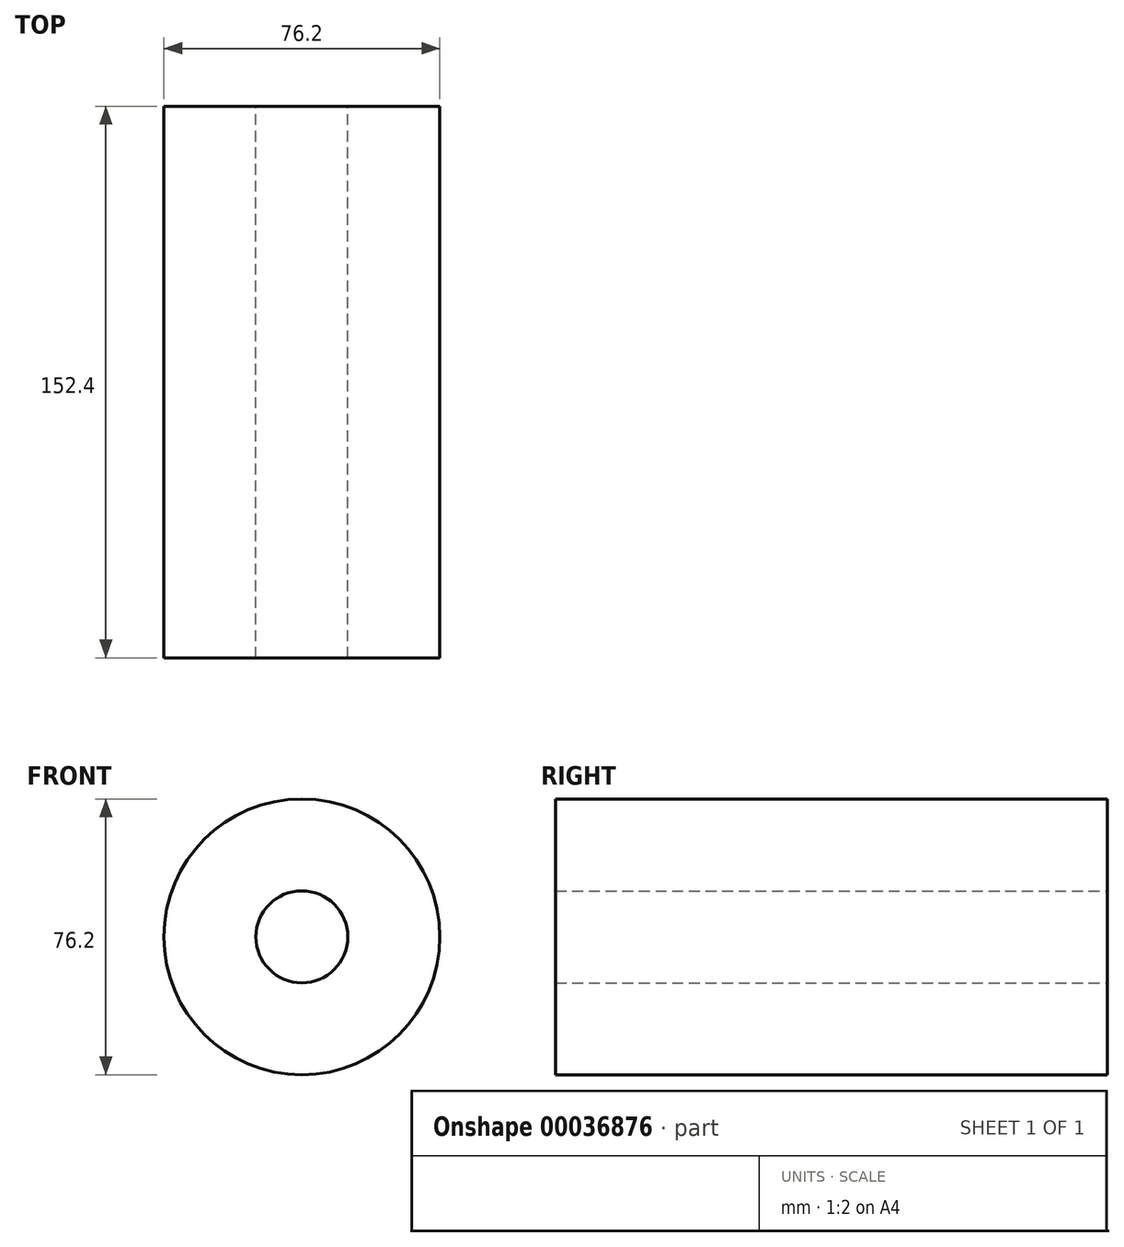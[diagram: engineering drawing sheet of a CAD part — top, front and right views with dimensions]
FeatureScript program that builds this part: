
annotation { "Feature Type Name" : "Feature", "Feature Type Description" : "" }
export const myFeature = defineFeature(function(context is Context, id is Id, definition is map)
    precondition{}
    {
        {
            var Q0;
            Q0=qCreatedBy(makeId("Front.planeOp"),FACE);
            var sketch = newSketch(context, id + "F0", { "sketchPlane" : qUnion([Q0])});
            skCircle(sketch, "E0", {"center": v(0, 0) * mm, "radius": 12.7 * mm});
            skCircle(sketch, "E1", {"center": v(0, 0) * mm, "radius": 38.1 * mm});
            skSolve(sketch);
        }
        {
            var Q0;
            Q0=makeQuery(id+"F0.imprint","IMPRINT",FACE,{"disambiguationData":[TD([[makeQuery(id+"F0.imprint","IMPRINT",EDGE,{"derivedFrom":sQuery(id+"F0.wireOp",EDGE,"E0")}),-1.0]])]});
            extrude(context, id + "F1", {"entities" : qUnion([Q0]), "depth" : 152.4 * mm});
        }
    });
